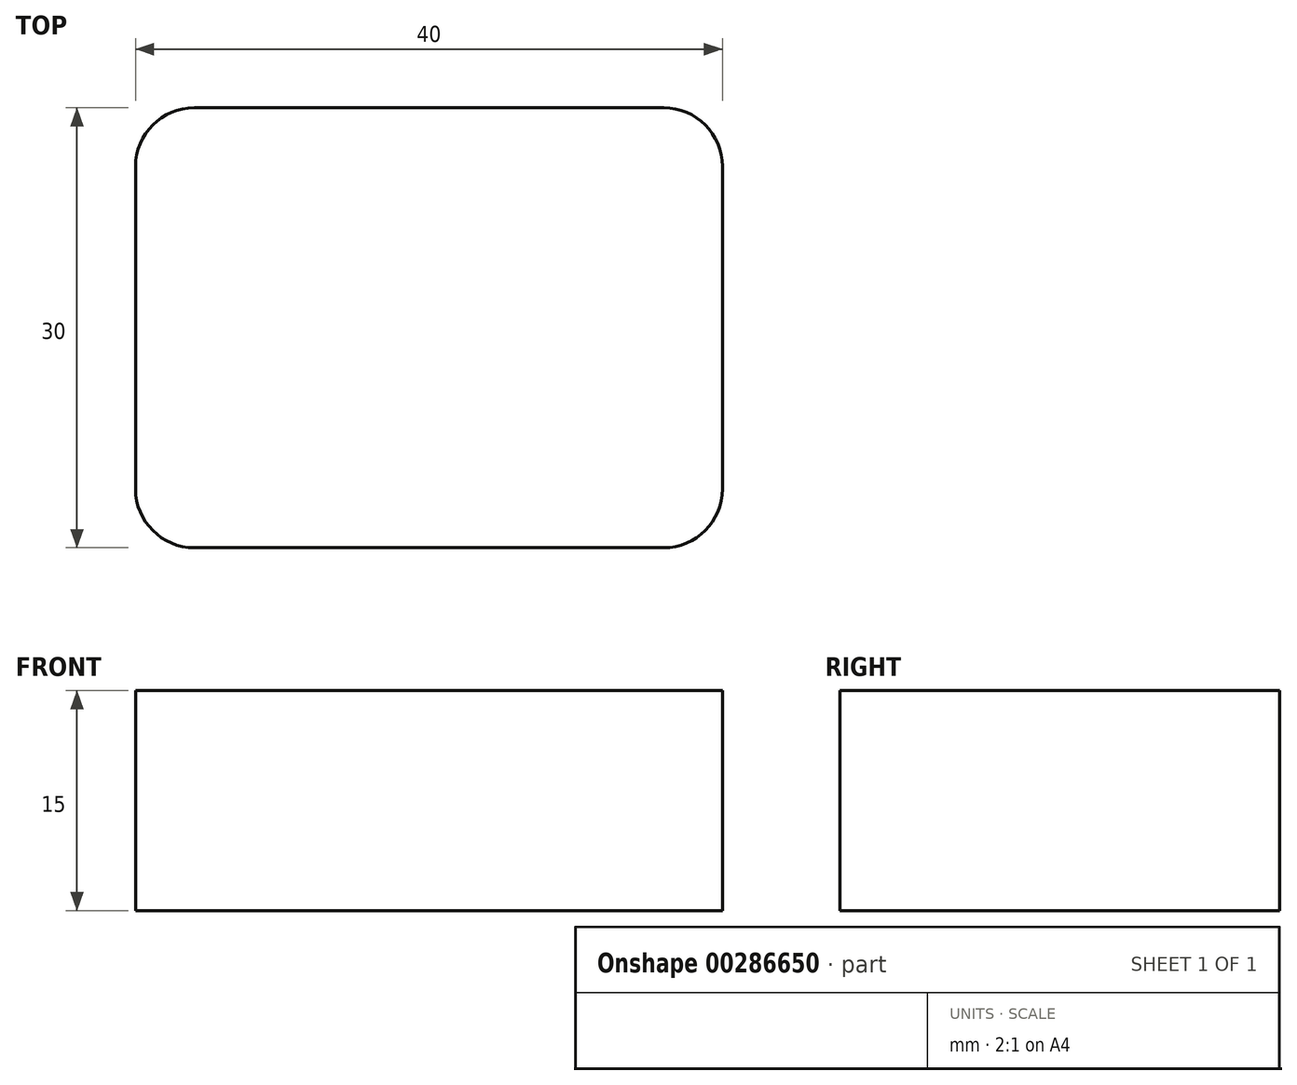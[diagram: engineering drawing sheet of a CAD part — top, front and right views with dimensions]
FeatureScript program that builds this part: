
annotation { "Feature Type Name" : "Feature", "Feature Type Description" : "" }
export const myFeature = defineFeature(function(context is Context, id is Id, definition is map)
    precondition{}
    {
        {
            var Q0;
            Q0=qCreatedBy(makeId("Top.planeOp"),FACE);
            var sketch = newSketch(context, id + "F0", { "sketchPlane" : qUnion([Q0])});
            skLineSegment(sketch, "E0.bottom", {"start": v(16, 15) * mm, "end": v(-16, 15) * mm});
            skLineSegment(sketch, "E0.top", {"start": v(16, -15) * mm, "end": v(-16, -15) * mm});
            skLineSegment(sketch, "E0.left", {"start": v(20, 11) * mm, "end": v(20, -11) * mm});
            skLineSegment(sketch, "E0.right", {"start": v(-20, 11) * mm, "end": v(-20, -11) * mm});
            skPoint(sketch, "E0.middle", {"position": v(0, 0) * mm});
            skPoint(sketch, "E1.visualSharp", {"position": v(-20, 15) * mm});
            skArc(sketch, "E1.filletArc", {"start": v(-16, 15) * mm, "mid": v(-18.83, 13.83) * mm, "end": v(-20, 11) * mm});
            skPoint(sketch, "E2.visualSharp", {"position": v(20, 15) * mm});
            skArc(sketch, "E2.filletArc", {"start": v(20, 11) * mm, "mid": v(18.83, 13.83) * mm, "end": v(16, 15) * mm});
            skPoint(sketch, "E3.visualSharp", {"position": v(20, -15) * mm});
            skArc(sketch, "E3.filletArc", {"start": v(16, -15) * mm, "mid": v(18.83, -13.83) * mm, "end": v(20, -11) * mm});
            skPoint(sketch, "E4.visualSharp", {"position": v(-20, -15) * mm});
            skArc(sketch, "E4.filletArc", {"start": v(-20, -11) * mm, "mid": v(-18.83, -13.83) * mm, "end": v(-16, -15) * mm});
            skSolve(sketch);
        }
        {
            var Q0;
            Q0=makeQuery(id+"F0.imprint","IMPRINT",FACE,{"disambiguationData":[TD([[makeQuery(id+"F0.imprint","IMPRINT",EDGE,{"derivedFrom":sQuery(id+"F0.wireOp",EDGE,"E0.bottom")}),1.0]])]});
            extrude(context, id + "F1", {"entities" : qUnion([Q0]), "depth" : 15 * mm});
        }
    });
